# Revit family: 51792221
name_source: partatom
category: Plumbing Fixtures
units: mm (PartAtom-declared; Revit-internal decimal feet)

## family parameters
Always vertical = Yes
Cut with Voids When Loaded = No
OmniClass Number = 23.45.55.00
OmniClass Title = Sanitary Faucets, Wastes
Part Type = Normal
Room Calculation Point = No
Round Connector Dimension = Use Diameter
Shared = No
Work Plane-Based = No

## types (1)
- 51792221 Washbasin faucet, 9/12 V, Bluetooth
    2D/3D/BIM Files URL = http://static.hansa.com
    3D View = https://static.hansa.com
    Advanced Features = Inner body made of DZR brass;3S-installation system for safe and simple mounting;Software settings adjustable via App
    Aerator = Hidden aerator
    Afterflow Period = 3 s (1-20 s)
    Ambience photo = http://static.hansa.com
    Approval DVGW = CW-6514CR0161
    AssetType = Fixed
    Automatic Flush Frequency = off (off/1-120 h)
    Automatic Flush Period = 30 s (1-1800 s)
    BIMObjectName = 51792221(2020)
    Backflow Prevention EN1717 = AA
    Bluetooth = 4.x (D034445)
    BodyMaterial = Brass
    Brand = HANSA
    Catalog Drawing URL = http://static.hansa.com
    Category = Washbasin
    CloseOffRating = 0
    Color = Chrome
    Connection = Flexible inlet pipes
    Connection Size = G3/8
    Default Elevation = 0 mm  [stored 0 ft]
    Dimension Drawing URL = http://static.hansa.com
    DurationUnit = Year
    EAN Number = 4057304006593
    EMC Directive = Radio Equipment Directive 2014/53/EU , 
Low Voltage Directive 2014/35/EU , 
EMC Directive 2014/30/EU , 
RoHS Directive 2011/65/EU
    EN Standard = EN 15091,
ETSI EN 301 489-1 V1.9.2 , 
ETSI EN 300 328 v2.2.2 , 
EN 61000-6-1:2007 , 
EN 61000-6-3:2007+A1:2011+AC:2012 , 
EN 60335-1:2012+A11+A13+A1+A14+A2+A15:2021, Part 19.11.4
    ETIM Class Number = EC010340 Electronic tap
    Electrical Connection = 230 / 9 V
    Electronic Parts = Autofocus infrared sensor;Power supply
    Excluded Items = Without draw-rod opening
    Extensions = Push pop-up waste without draw-rod
    FDV Document URL = http://www.hansa.com
    FaucetMainMaterial = Brass
    Features = Touchless;Plug transformer;Bluetooth®
    Finish = Polished
    Flow Drawing URL = http://static.hansa.com
    Flow Rate At 300kPa With Flow Controller = 0.1 L/s
    FlowCoefficient = 0
    Group = Washbasin faucet
    IfcExportAs = IfcValveType
    IfcExportType = FAUCET
    InletConnectionSize = 10 mm  [stored 0.0328084 ft]
    Installation Type = Deck mounted
    Installation and Maintenance Guide URL = http://static.hansa.com
    Interactive AR View URL = https://static.hansa.com
    Lever Handle = Temperature control handle
    Long Marketing = electronic basin faucet, DN 15
    Manufacturer = HANSA
    ManufacturerName = HANSA
    ManufacturerURL = http://www.hansa.com
    Market = International;Germany;Austria;Belgium;Netherlands;France;Czech Republic;Slovakia;Spain
    Material = Brass
    Max Flow Period = 2 min (1 - 1800 s)
    Max. Hot Water Supply = 70 °C
    Mechanical Parts = Mixing valve for manual temperature control;Non-return valve(s);Litter filter(s)
    Mobile Product Information URL = http://mpi.hansa.com
    Model = 51792221 Washbasin faucet, 9/12 V, Bluetooth
    ModelReference = 51792221
    Mounting Holes = 1 hole
    NBSDescription = Water supply fittings for wash basins and troughs
    NBSReference = 45-35-70/371
    Name = 51792221 Washbasin faucet, 9/12 V, Bluetooth
    Name_en = 51792221 Washbasin faucet, 9/12 V, Bluetooth
    Noise Class = I (ISO 3822)
    NominalDepth = 187 mm  [stored 0.613517 ft]
    NominalHeight = 196 mm  [stored 0.643045 ft]
    NominalWidth = 70 mm
    Operating Distance = 20-130 mm (110/130/160 mm)
    Operating Voltage = 912 V
    Pressure Loss With Flow 01ls = 200000.0 Pa
    Product Code = 51792221
    Product Family = HANSADESIGNO Style
    Product Image URL = http://static.hansa.com
    Product URL = http://static.hansa.com
    Protection Class = IP 55 / transformer IP 20
    Sales Package dimensions (LxWxH) = 370 x 192 x 90
    Shape = Sculptured
    Size = 70x187x196 mm
    Spare-Part Information URL = http://static.hansa.com
    Spout Projection = 138 mm
    Spout Type = Fixed spout
    Surface treatment = Chrome
    Technical DataSheet URL = http://www.hansa.com
    Temperature = Temperature limiter (retrofittable)
    Temperature Adjustments = Adjustable hot water stop (included, retrofittable)
    UNSPSC Class Number = 30181700 Faucets or taps
    URL DVGW = http://static.hansa.com
    URL Declaration Of Performance (DOP) = http://static.hansa.com
    URL Declaration of Asbestos = http://static.hansa.com
    URL Declaration of Conformity = http://static.hansa.com
    URL Declaration of SCIP = http://static.hansa.com
    URL EU Packaging Declaration = http://static.hansa.com
    URL EcoLabel Declaration = http://static.hansa.com
    URL REACH = http://static.hansa.com
    URL WEEE = http://static.hansa.com
    Uniclass2 = Pr_40_30_96_96
    Uniclass2015Description = Washbasin manual water supply sets
    Uniclass2015Reference = Pr_40_20_87_96
    Version = 1
    VersionDate = 01/06/2023
    Warranty Information URL = http://warranty.hansa.com
    WarrantyDescription = http://warranty.hansa.com
    WarrantyDurationUnit = Year
    Working Pressure = 100 - 1000 kPa

note: [stored X ft] marks values corroborated as IEEE doubles in the binary element streams (Revit-internal decimal feet)

## geometry (parser evidence)
native form markers: Sweep x6
no freeform markers — native parametric forms only
